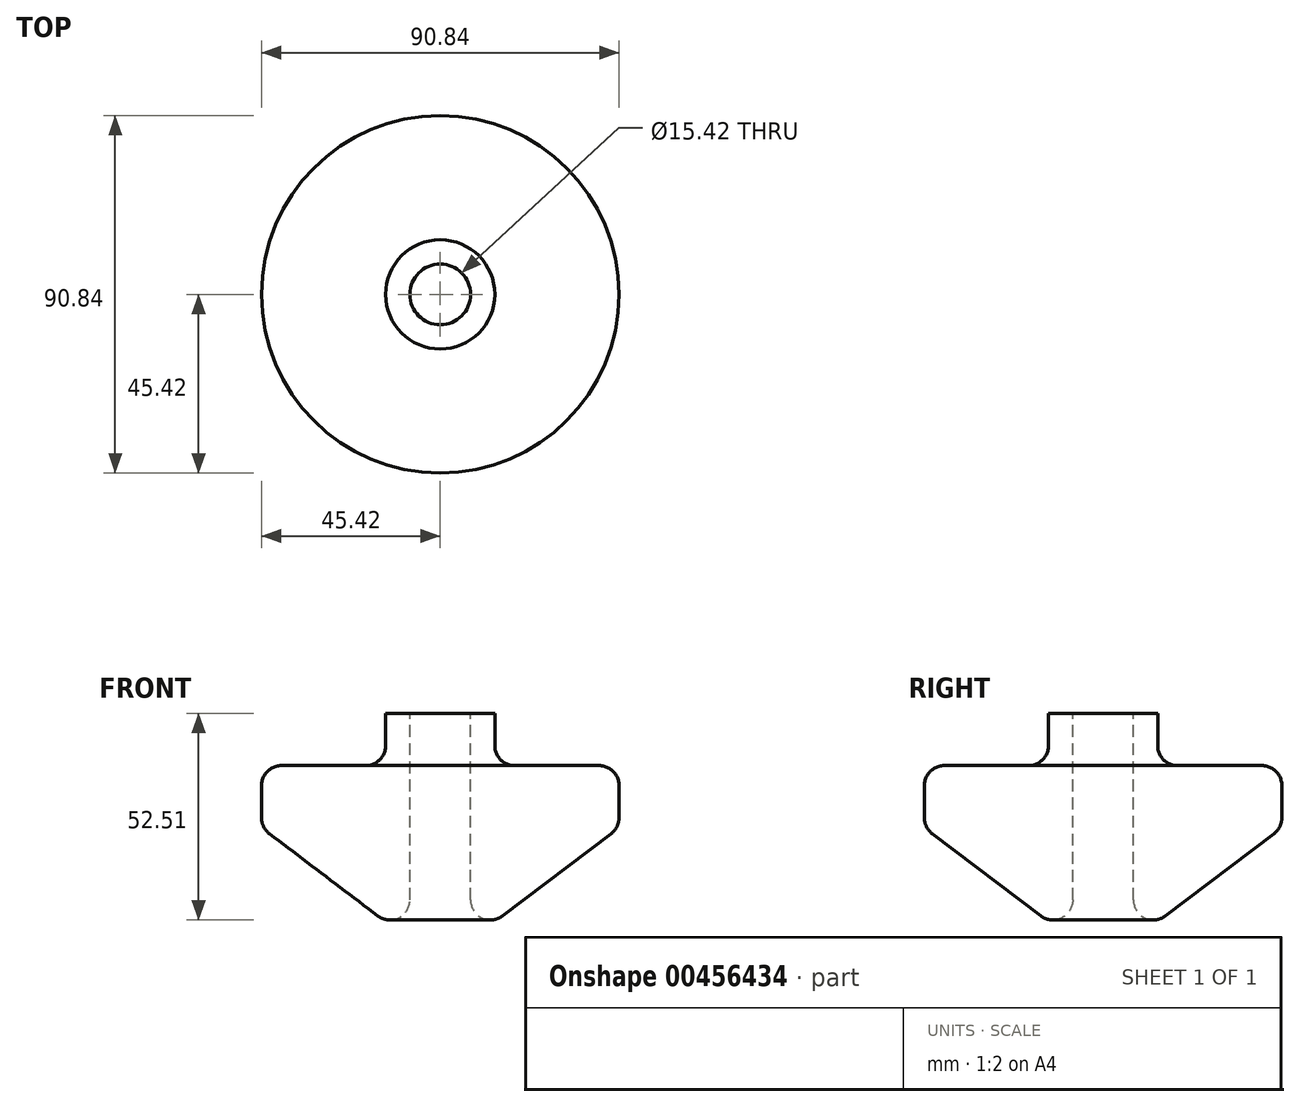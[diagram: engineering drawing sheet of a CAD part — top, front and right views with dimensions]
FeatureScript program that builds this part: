
annotation { "Feature Type Name" : "Feature", "Feature Type Description" : "" }
export const myFeature = defineFeature(function(context is Context, id is Id, definition is map)
    precondition{}
    {
        {
            var Q0;
            Q0=qCreatedBy(makeId("Front.planeOp"),FACE);
            var sketch = newSketch(context, id + "F0", { "sketchPlane" : qUnion([Q0])});
            skLineSegment(sketch, "E0", {"start": v(0, 0) * mm, "end": v(45.42, 34.42) * mm});
            skLineSegment(sketch, "E1", {"start": v(45.42, 34.42) * mm, "end": v(45.42, 50.2) * mm});
            skLineSegment(sketch, "E2", {"start": v(45.42, 50.2) * mm, "end": v(13.87, 50.2) * mm});
            skLineSegment(sketch, "E3", {"start": v(13.87, 50.2) * mm, "end": v(13.87, 63.5) * mm});
            skLineSegment(sketch, "E4", {"start": v(13.87, 63.5) * mm, "end": v(0, 63.5) * mm});
            skLineSegment(sketch, "E5", {"start": v(0, 63.5) * mm, "end": v(0, 0) * mm});
            skSolve(sketch);
        }
        {
            var Q0;
            Q0=qSketchRegion(id+"F0",true);
            var Q1;
            Q1=sQuery(id+"F0.wireOp",EDGE,"E5");
            revolve(context, id + "F1", {"entities" : qUnion([Q0]), "axis" : qUnion([Q1]), "revolveType" : RevolveType.FULL});
        }
        {
            var Q0;
            Q0=makeQuery(id+"F1.opRevolve","SWEPT_FACE",FACE,{"disambiguationData":[OSD([sQuery(id+"F0.wireOp",EDGE,"E4")])]});
            var sketch = newSketch(context, id + "F2", { "sketchPlane" : qUnion([Q0])});
            skCircle(sketch, "E6", {"center": v(0, 0) * mm, "radius": 7.7 * mm});
            skSolve(sketch);
        }
        {
            var Q0;
            Q0=makeQuery(id+"F2.imprint","IMPRINT",FACE,{"disambiguationData":[TD([[makeQuery(id+"F2.imprint","IMPRINT",EDGE,{"derivedFrom":sQuery(id+"F2.wireOp",EDGE,"E6")}),1.0]])]});
            extrude(context, id + "F3", {"entities" : qUnion([Q0]), "operationType" : NewBodyOperationType.REMOVE, "oppositeDirection" : true, "depth" : 88.9 * mm});
        }
        {
            var Q0;
            Q0=makeQuery(id+"F1.opRevolve","SWEPT_FACE",FACE,{"disambiguationData":[OSD([sQuery(id+"F0.wireOp",EDGE,"E2")])]});
            fillet(context, id + "F4", {"entities" : qUnion([Q0]), "radius" : 5.08 * mm, "tangentPropagation" : true, "allowEdgeOverflow" : false});
        }
        {
            var Q0;
            Q0=makeQuery(id+"F1.opRevolve","SWEPT_FACE",FACE,{"disambiguationData":[OSD([sQuery(id+"F0.wireOp",EDGE,"E0")])]});
            fillet(context, id + "F5", {"entities" : qUnion([Q0]), "radius" : 5.08 * mm, "tangentPropagation" : true, "allowEdgeOverflow" : false});
        }
    });
